# Revit family: EURS_63_LF_FB_Luxspace Recessed DN571B_PHI
name_source: partatom
category: Lighting Fixtures
revit_build: Autodesk Revit 2016 (Build: 20161004_0715(x64)
units: mm (PartAtom-declared; Revit-internal decimal feet)

## family parameters
Cut with Voids When Loaded = No
Host = Face
Light Source = No
Part Type = Normal
Room Calculation Point = No
Round Connector Dimension = Use Diameter
Shared = Yes

## types (1)
- Type catalog
    12NC = 910503592915
    Apparent Load = 18 VA
    BIM Library - URL = http://www.lighting.philips.com
    Ceiling thickness = 13 mm  [stored 0.0426509 ft]
    Content modified date = 03-04-2020
    Content version = 1.0
    Cut out diameter = 204 mm
    Default Elevation = 0 mm  [stored 0 ft]
    Description = Luxspace Recessed
    Diameter = 214 mm  [stored 0.7021 ft]
    EOC = EOC CODE
    ETIM code = EC002892
    ETIM code URL = https://prod.etim-international.com
    Fixture code = 871829193105800
    Height = 119 mm  [stored 0.39042 ft]
    Installation space height = 120 mm  [stored 0.393701 ft]
    Lamp = LAMP NAME
    Lamp type = DN571B IES Data : 1 xLED38S_TWH-5000 F
    Last IES update = DATE
    Length = 214 mm  [stored 0.7021 ft]
    Light source = 2 mm  [stored 0.00656168 ft]
    Manufacturer = Philips
    Model = DN571B
    Order code = 910503592915
    Product catalog - URL = https://www.lighting.philips.com
    Rim height = 3 mm  [stored 0.00984252 ft]
    Type Comments = Recessed
    URL = http://www.lighting.philips.com
    Voltage (V) = 230 V
    Width = 214 mm  [stored 0.7021 ft]

note: [stored X ft] marks values corroborated as IEEE doubles in the binary element streams (Revit-internal decimal feet)

## geometry (parser evidence)
native form markers: Blend x4, Sweep x17
no freeform markers — native parametric forms only
